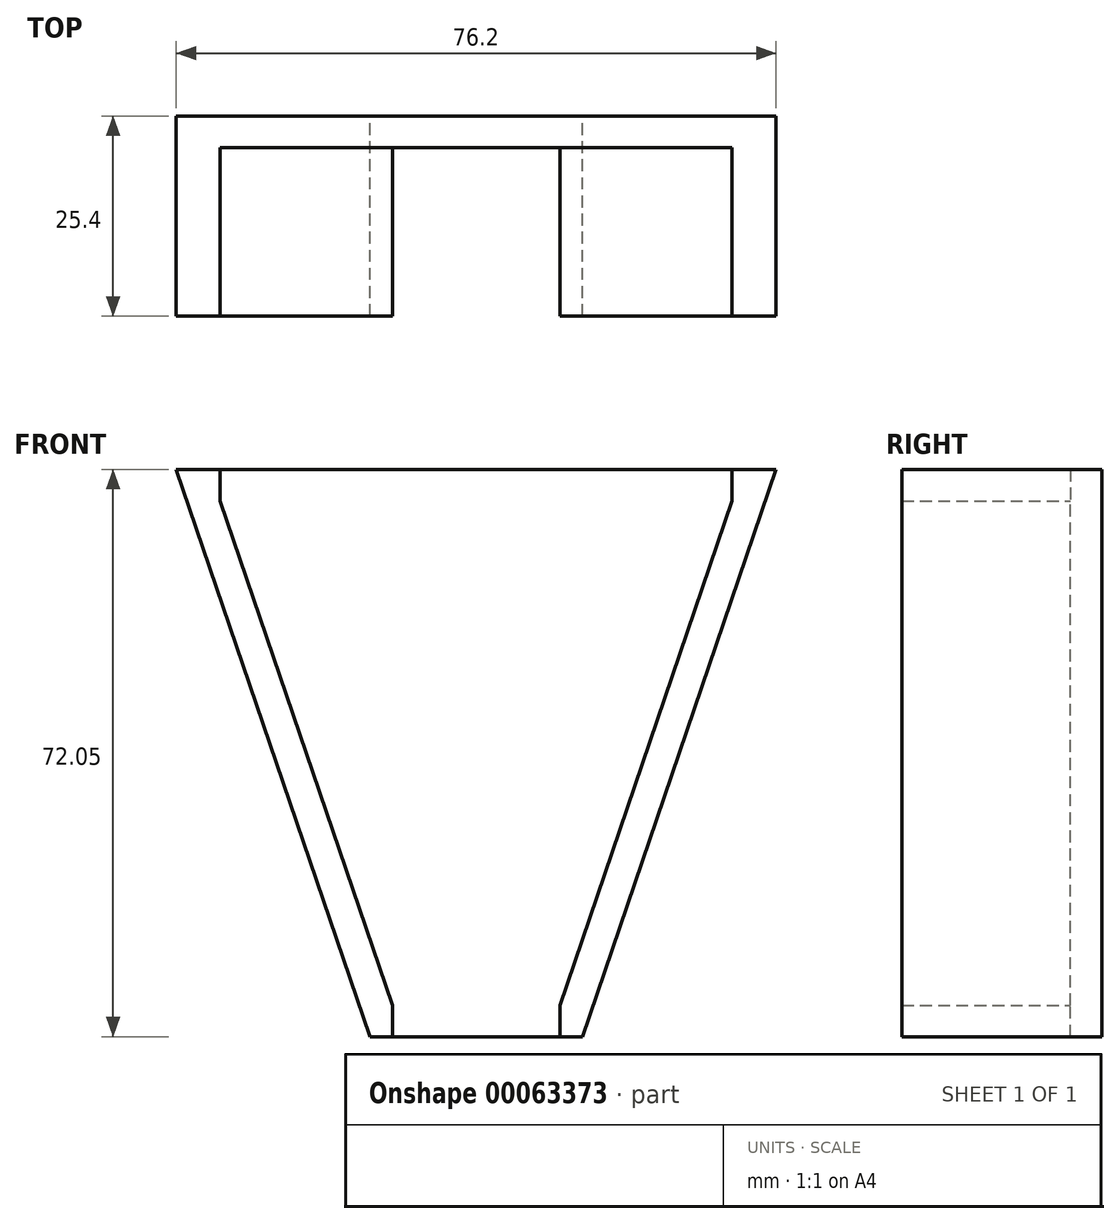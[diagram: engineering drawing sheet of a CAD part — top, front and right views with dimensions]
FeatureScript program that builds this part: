
annotation { "Feature Type Name" : "Feature", "Feature Type Description" : "" }
export const myFeature = defineFeature(function(context is Context, id is Id, definition is map)
    precondition{}
    {
        {
            var Q0;
            Q0=qCreatedBy(makeId("Front.planeOp"),FACE);
            var sketch = newSketch(context, id + "F0", { "sketchPlane" : qUnion([Q0])});
            skLineSegment(sketch, "E0", {"start": v(13.5, -32.9) * mm, "end": v(38.1, 39.16) * mm});
            skLineSegment(sketch, "E1", {"start": v(38.1, 39.16) * mm, "end": v(0, 39.16) * mm});
            skLineSegment(sketch, "E2", {"start": v(13.5, -32.9) * mm, "end": v(0, -32.9) * mm});
            skLineSegment(sketch, "E3.MirrorCS", {"start": v(-38.1, 39.16) * mm, "end": v(0, 39.16) * mm});
            skLineSegment(sketch, "E4.MirrorCS", {"start": v(-13.5, -32.9) * mm, "end": v(-38.1, 39.16) * mm});
            skLineSegment(sketch, "E5.MirrorCS", {"start": v(-13.5, -32.9) * mm, "end": v(0, -32.9) * mm});
            skSolve(sketch);
        }
        {
            var Q0;
            Q0=makeQuery(id+"F0.imprint","IMPRINT",FACE,{"disambiguationData":[TD([[makeQuery(id+"F0.imprint","IMPRINT",EDGE,{"derivedFrom":sQuery(id+"F0.wireOp",EDGE,"E0")}),1.0]])]});
            extrude(context, id + "F1", {"entities" : qUnion([Q0]), "depth" : 25.4 * mm});
        }
        {
            var Q0;
            Q0=makeQuery(id+"F1.opExtrude","CAP_FACE",FACE,{"disambiguationData":[OSD([sQuery(id+"F0.wireOp",EDGE,"E0"),sQuery(id+"F0.wireOp",EDGE,"E1"),sQuery(id+"F0.wireOp",EDGE,"E2"),sQuery(id+"F0.wireOp",EDGE,"E3.MirrorCS"),sQuery(id+"F0.wireOp",EDGE,"E4.MirrorCS"),sQuery(id+"F0.wireOp",EDGE,"E5.MirrorCS")])],"isStart":false});
            shell(context, id + "F2", {"entities" : qUnion([Q0]), "thickness" : 4 * mm});
        }
        {
            var Q0;
            Q0=makeQuery(id+"F2.opShell","OFFSET_FACE",FACE,{"disambiguationData":[OSD([sQuery(id+"F0.wireOp",EDGE,"E2"),sQuery(id+"F0.wireOp",EDGE,"E5.MirrorCS")])]});
            extrude(context, id + "F3", {"entities" : qUnion([Q0]), "operationType" : NewBodyOperationType.REMOVE, "endBound" : BoundingType.UP_TO_NEXT, "oppositeDirection" : true, "depth" : 25.4 * mm});
        }
        {
            var Q0;
            Q0=makeQuery(id+"F2.opShell","OFFSET_FACE",FACE,{"disambiguationData":[OSD([sQuery(id+"F0.wireOp",EDGE,"E1"),sQuery(id+"F0.wireOp",EDGE,"E3.MirrorCS")])]});
            extrude(context, id + "F4", {"entities" : qUnion([Q0]), "operationType" : NewBodyOperationType.REMOVE, "endBound" : BoundingType.UP_TO_NEXT, "oppositeDirection" : true, "depth" : 25.4 * mm});
        }
    });
